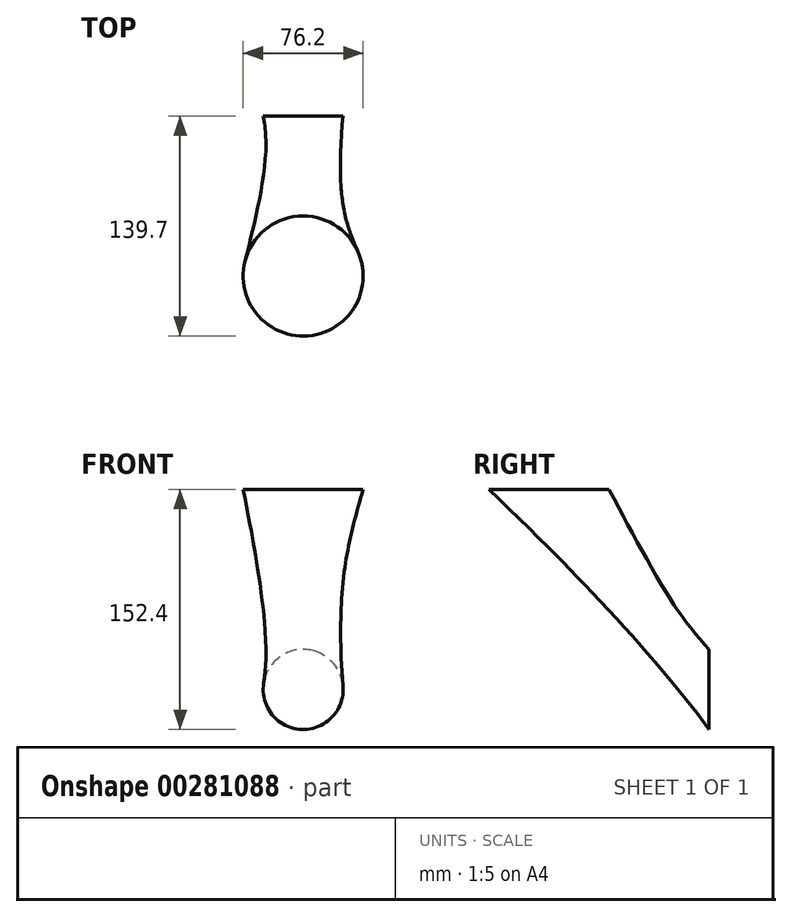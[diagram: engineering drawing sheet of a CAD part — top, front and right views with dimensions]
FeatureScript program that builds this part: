
annotation { "Feature Type Name" : "Feature", "Feature Type Description" : "" }
export const myFeature = defineFeature(function(context is Context, id is Id, definition is map)
    precondition{}
    {
        {
            var Q0;
            Q0=qCreatedBy(makeId("Front.planeOp"),FACE);
            var sketch = newSketch(context, id + "F0", { "sketchPlane" : qUnion([Q0])});
            skCircle(sketch, "E0", {"center": v(0, 0) * mm, "radius": 25.4 * mm});
            skSolve(sketch);
        }
        {
            var Q0;
            Q0=qCreatedBy(makeId("Top.planeOp"),FACE);
            cPlane(context, id + "F1", {"entities" : qUnion([Q0]), "cplaneType" : CPlaneType.OFFSET, "offset" : 127 * mm, "width" : 152.4 * mm, "height" : 152.4 * mm});
        }
        {
            var Q0;
            Q0=qCreatedBy(id+"F1.planeOp",FACE);
            var sketch = newSketch(context, id + "F2", { "sketchPlane" : qUnion([Q0])});
            skLineSegment(sketch, "E1", {"start": v(0, 0) * mm, "end": v(0, -101.6) * mm, "construction": true});
            skCircle(sketch, "E2", {"center": v(0, -101.6) * mm, "radius": 38.1 * mm});
            skSolve(sketch);
        }
        {
            var Q0;
            Q0=makeQuery(id+"F2.imprint","IMPRINT",FACE,{"disambiguationData":[TD([[makeQuery(id+"F2.imprint","IMPRINT",EDGE,{"derivedFrom":sQuery(id+"F2.wireOp",EDGE,"E2")}),1.0]])]});
            var Q1;
            Q1=makeQuery(id+"F0.imprint","IMPRINT",FACE,{"disambiguationData":[TD([[makeQuery(id+"F0.imprint","IMPRINT",EDGE,{"derivedFrom":sQuery(id+"F0.wireOp",EDGE,"E0")}),1.0]])]});
            loft(context, id + "F3", {"sheetProfilesArray" : [{ "sheetProfileEntities" : qUnion([Q0]) }, { "sheetProfileEntities" : qUnion([Q1]) }]});
        }
    });
